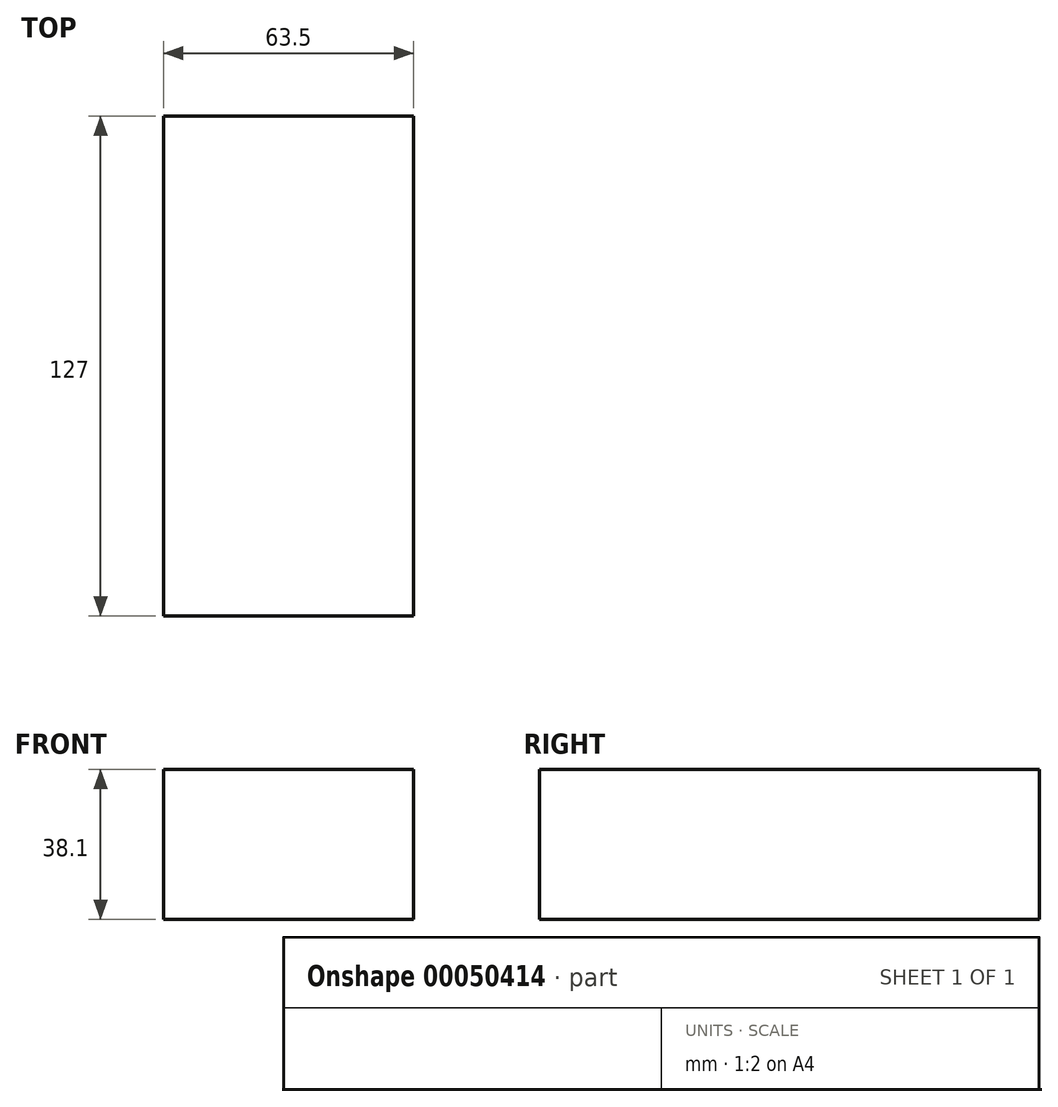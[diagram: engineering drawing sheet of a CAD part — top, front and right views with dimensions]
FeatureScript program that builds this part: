
annotation { "Feature Type Name" : "Feature", "Feature Type Description" : "" }
export const myFeature = defineFeature(function(context is Context, id is Id, definition is map)
    precondition{}
    {
        {
            var Q0;
            Q0=qCreatedBy(makeId("Front.planeOp"),FACE);
            var sketch = newSketch(context, id + "F0", { "sketchPlane" : qUnion([Q0])});
            skLineSegment(sketch, "E0.bottom", {"start": v(0, 0) * mm, "end": v(63.5, 0) * mm});
            skLineSegment(sketch, "E0.top", {"start": v(0, 38.1) * mm, "end": v(63.5, 38.1) * mm});
            skLineSegment(sketch, "E0.left", {"start": v(0, 0) * mm, "end": v(0, 38.1) * mm});
            skLineSegment(sketch, "E0.right", {"start": v(63.5, 0) * mm, "end": v(63.5, 38.1) * mm});
            skSolve(sketch);
        }
        {
            var Q0;
            Q0 = qSketchRegion(id + "F0", true);
            extrude(context, id + "F1", {"entities" : qUnion([Q0]), "depth" : 127 * mm});
        }
    });
